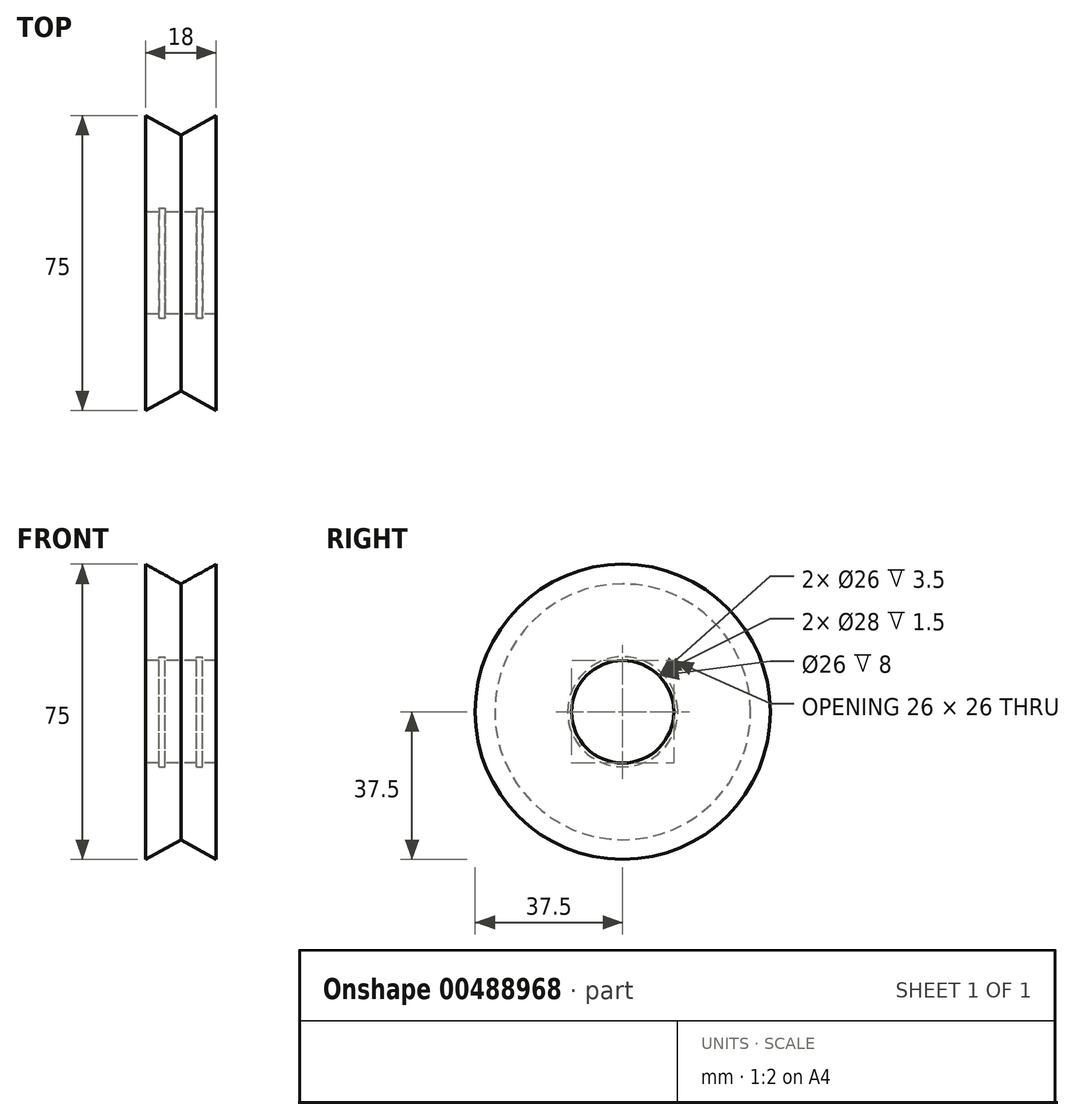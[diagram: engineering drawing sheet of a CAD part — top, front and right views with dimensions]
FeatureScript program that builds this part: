
annotation { "Feature Type Name" : "Feature", "Feature Type Description" : "" }
export const myFeature = defineFeature(function(context is Context, id is Id, definition is map)
    precondition{}
    {
        {
            var Q0;
            Q0=qCreatedBy(makeId("Top.planeOp"),FACE);
            var sketch = newSketch(context, id + "F0", { "sketchPlane" : qUnion([Q0])});
            skLineSegment(sketch, "E0", {"start": v(0, 47.97) * mm, "end": v(0, -45.27) * mm, "construction": true});
            skLineSegment(sketch, "E1", {"start": v(-40.81, 0) * mm, "end": v(48.24, 0) * mm, "construction": true});
            skLineSegment(sketch, "E2", {"start": v(-9, 13) * mm, "end": v(-9, 37.5) * mm});
            skLineSegment(sketch, "E3", {"start": v(-9, 37.5) * mm, "end": v(0, 32.5) * mm});
            skLineSegment(sketch, "E4.MirrorCS", {"start": v(9, 37.5) * mm, "end": v(0, 32.5) * mm});
            skLineSegment(sketch, "E5.MirrorCS", {"start": v(9, 13) * mm, "end": v(9, 37.5) * mm});
            skPoint(sketch, "E6.end.orphan", {"position": v(0, 6) * mm});
            skLineSegment(sketch, "E7", {"start": v(9, 13) * mm, "end": v(-9, 13) * mm});
            skPoint(sketch, "E8.MirrorCS.end.orphan", {"position": v(9, 13) * mm});
            skSolve(sketch);
        }
        {
            var Q0;
            Q0=makeQuery(id+"F0.imprint","IMPRINT",FACE,{"disambiguationData":[TD([[makeQuery(id+"F0.imprint","IMPRINT",EDGE,{"derivedFrom":sQuery(id+"F0.wireOp",EDGE,"E2")}),-1.0]])]});
            var Q1;
            Q1=sQuery(id+"F0.wireOp",EDGE,"E1");
            revolve(context, id + "F1", {"entities" : qUnion([Q0]), "axis" : qUnion([Q1]), "revolveType" : RevolveType.FULL});
        }
        {
            var Q0;
            Q0=qCreatedBy(makeId("Top.planeOp"),FACE);
            var sketch = newSketch(context, id + "F2", { "sketchPlane" : qUnion([Q0])});
            skLineSegment(sketch, "E9", {"start": v(-5.5, 13) * mm, "end": v(-5.5, 14) * mm});
            skLineSegment(sketch, "E10", {"start": v(-5.5, 14) * mm, "end": v(-4, 14) * mm});
            skLineSegment(sketch, "E11", {"start": v(-4, 14) * mm, "end": v(-4, 13) * mm});
            skLineSegment(sketch, "E12", {"start": v(-5.5, 13) * mm, "end": v(-4, 13) * mm});
            skLineSegment(sketch, "E13", {"start": v(-29.15, 0) * mm, "end": v(31.02, 0) * mm, "construction": true});
            skLineSegment(sketch, "E14.MirrorCS", {"start": v(5.5, 14) * mm, "end": v(4, 14) * mm});
            skLineSegment(sketch, "E15.MirrorCS", {"start": v(5.5, 13) * mm, "end": v(4, 13) * mm});
            skLineSegment(sketch, "E16.MirrorCS", {"start": v(5.5, 13) * mm, "end": v(5.5, 14) * mm});
            skLineSegment(sketch, "E17.MirrorCS", {"start": v(4, 14) * mm, "end": v(4, 13) * mm});
            skSolve(sketch);
        }
        {
            var Q0;
            Q0 = qSketchRegion(id + "F2", true);
            var Q1;
            Q1=sQuery(id+"F0.wireOp",EDGE,"E1");
            revolve(context, id + "F3", {"operationType" : NewBodyOperationType.REMOVE, "entities" : qUnion([Q0]), "axis" : qUnion([Q1]), "revolveType" : RevolveType.FULL, "oppositeDirection" : true});
        }
    });
